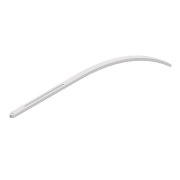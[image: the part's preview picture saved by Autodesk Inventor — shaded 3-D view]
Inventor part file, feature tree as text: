
AUTODESK INVENTOR PART (.ipt)
format: ipt  version: 2022 (Build 260153000, 153)  size: 123,392 bytes
history: native  units: mm
features: extrude x2, sketch x2, projected_geometry x2, fillet x1
ambient origin geometry x8: Origin, YZ Plane, XZ Plane, XY Plane, X Axis, Y Axis, Z Axis, Center Point
bodies: Solid1 (feature_tree)
feature tree (7):
  extrude  "Extrusion1"  Depth=10.0mm
  extrude  "Extrusion2"  Depth=2.0mm
  fillet  "Fillet1"  Radius=120.0mm
  sketch  "Sketch1"  dims[d0=160.0mm d1=10.0mm]
  sketch  "Sketch2"  dims[d2=3.3mm d3=30.0mm d5=120.0mm d6=3.3mm d7=6.0mm d8=0.0mm d9=6.0mm d10=373.775mm d11=90.0mm d12=10.0mm d13=0.0mm d14=2.0mm]
  projected_geometry  "Projected Loop1"
  projected_geometry  "Projected Loop2"
